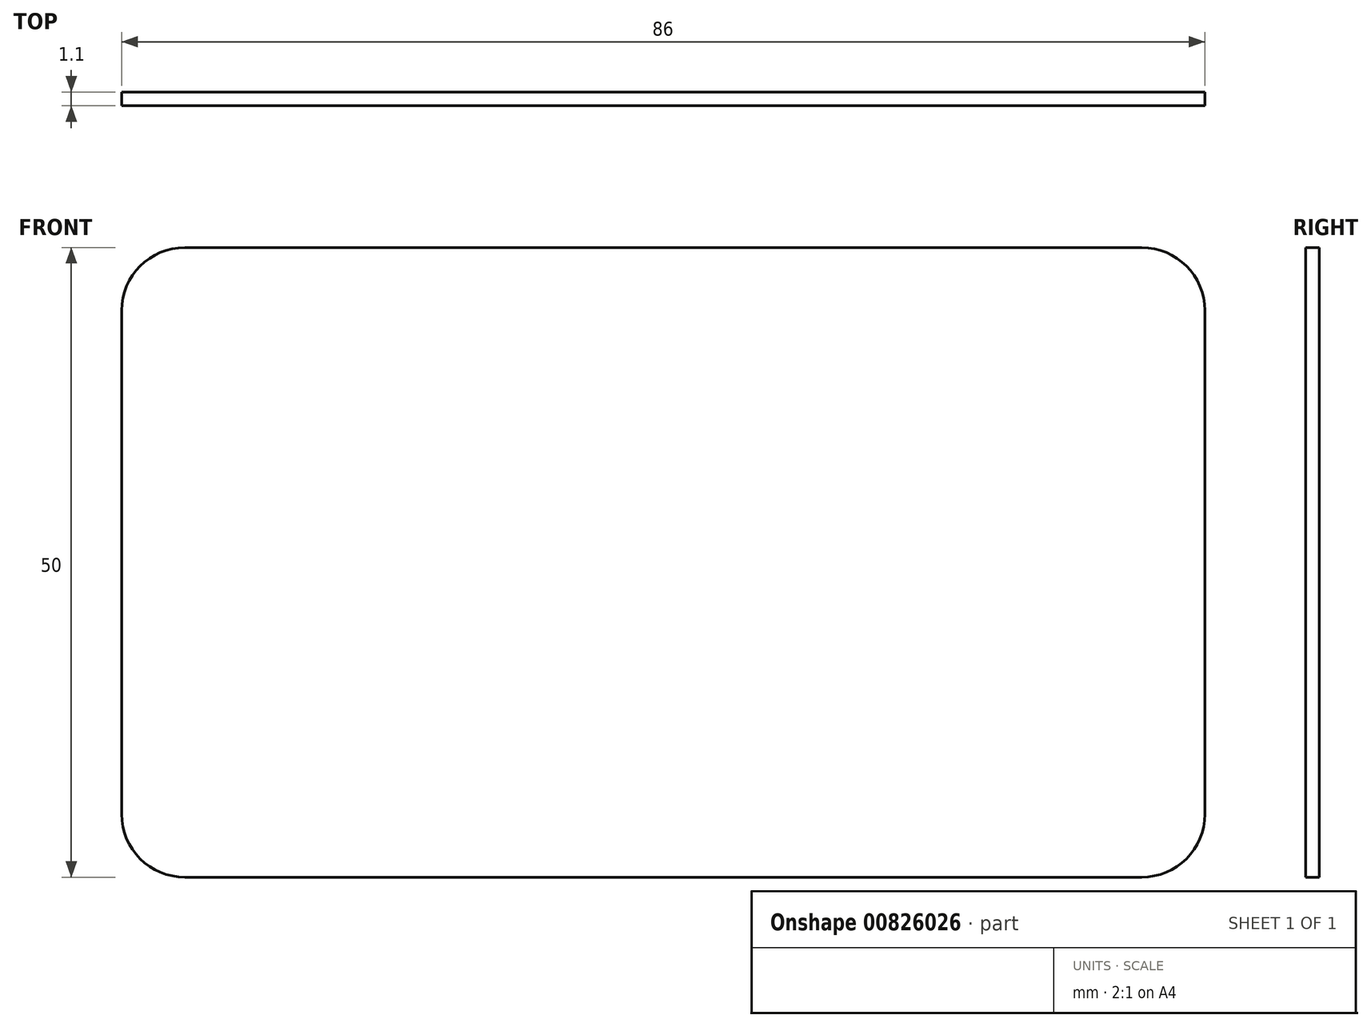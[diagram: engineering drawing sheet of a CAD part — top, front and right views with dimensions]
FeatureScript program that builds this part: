
annotation { "Feature Type Name" : "Feature", "Feature Type Description" : "" }
export const myFeature = defineFeature(function(context is Context, id is Id, definition is map)
    precondition{}
    {
        {
            var Q0;
            Q0=qCreatedBy(makeId("Front.planeOp"),FACE);
            var sketch = newSketch(context, id + "F0", { "sketchPlane" : qUnion([Q0])});
            skLineSegment(sketch, "E0.bottom", {"start": v(-52.44, 36.54) * mm, "end": v(23.56, 36.54) * mm});
            skLineSegment(sketch, "E0.top", {"start": v(-52.44, -13.46) * mm, "end": v(23.56, -13.46) * mm});
            skLineSegment(sketch, "E0.left", {"start": v(-57.44, 31.54) * mm, "end": v(-57.44, -8.46) * mm});
            skLineSegment(sketch, "E0.right", {"start": v(28.56, 31.54) * mm, "end": v(28.56, -8.46) * mm});
            skPoint(sketch, "E1.visualSharp", {"position": v(-57.44, 36.54) * mm});
            skArc(sketch, "E1.filletArc", {"start": v(-52.44, 36.54) * mm, "mid": v(-55.98, 35.07) * mm, "end": v(-57.44, 31.54) * mm});
            skPoint(sketch, "E2.visualSharp", {"position": v(28.56, 36.54) * mm});
            skArc(sketch, "E2.filletArc", {"start": v(28.56, 31.54) * mm, "mid": v(27.1, 35.07) * mm, "end": v(23.56, 36.54) * mm});
            skPoint(sketch, "E3.visualSharp", {"position": v(28.56, -13.46) * mm});
            skArc(sketch, "E3.filletArc", {"start": v(23.56, -13.46) * mm, "mid": v(27.1, -12) * mm, "end": v(28.56, -8.46) * mm});
            skPoint(sketch, "E4.visualSharp", {"position": v(-57.44, -13.46) * mm});
            skArc(sketch, "E4.filletArc", {"start": v(-57.44, -8.46) * mm, "mid": v(-55.98, -12) * mm, "end": v(-52.44, -13.46) * mm});
            skSolve(sketch);
        }
        {
            var Q0;
            Q0 = qSketchRegion(id + "F0", true);
            extrude(context, id + "F1", {"entities" : qUnion([Q0]), "depth" : 1.1 * mm, "offsetDistance" : 25 * mm});
        }
    });
